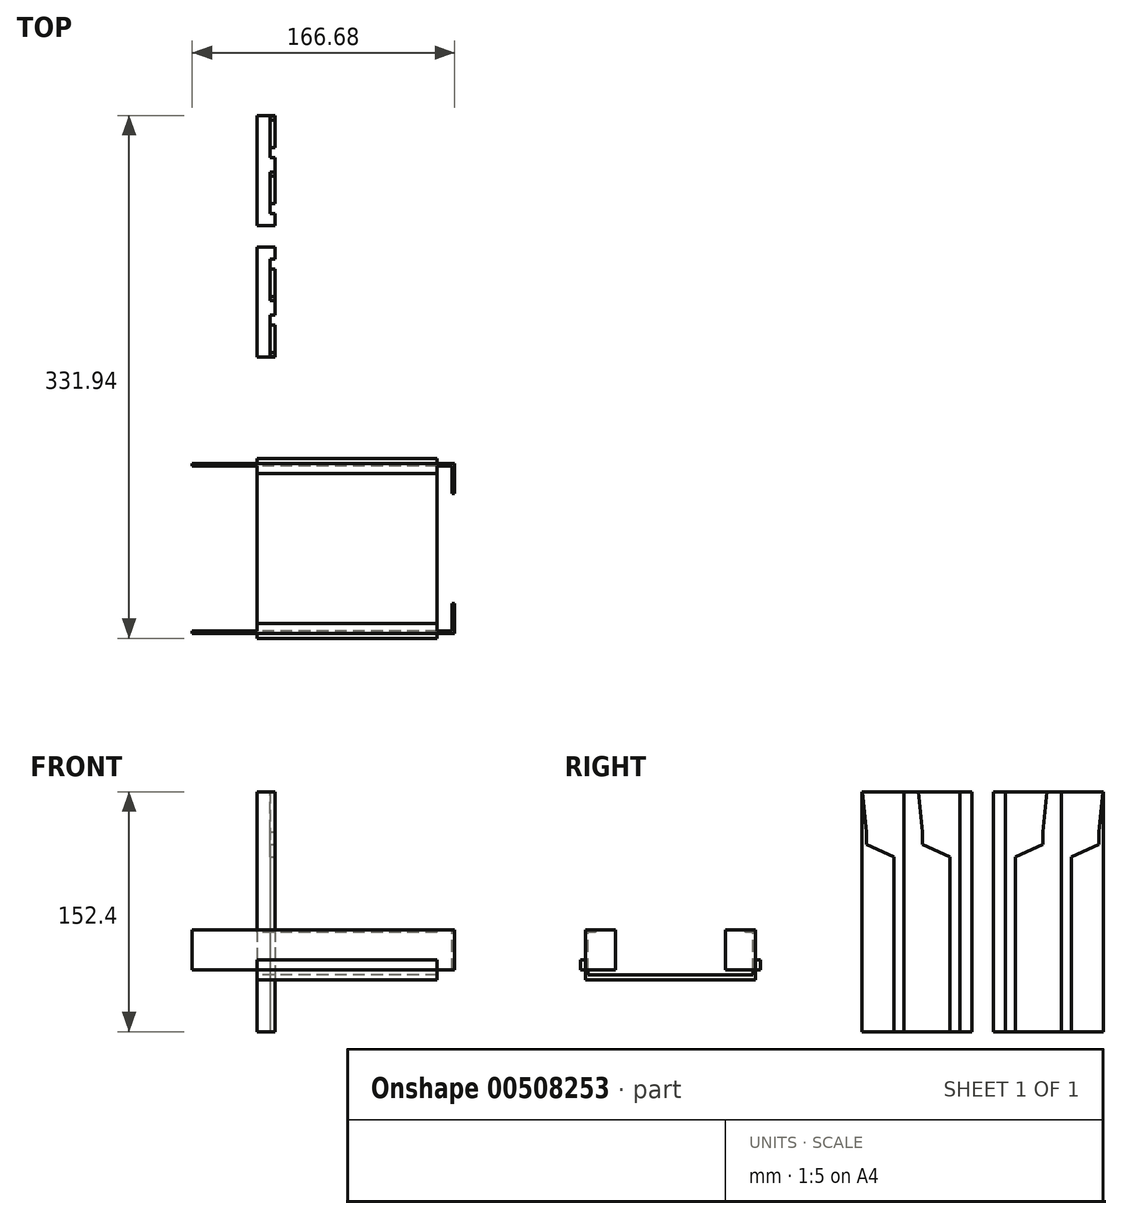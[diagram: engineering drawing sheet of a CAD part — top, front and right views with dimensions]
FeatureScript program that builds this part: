
annotation { "Feature Type Name" : "Feature", "Feature Type Description" : "" }
export const myFeature = defineFeature(function(context is Context, id is Id, definition is map)
    precondition{}
    {
        {
            var Q0;
            Q0=qCreatedBy(makeId("Right.planeOp"),FACE);
            var sketch = newSketch(context, id + "F0", { "sketchPlane" : qUnion([Q0])});
            skLineSegment(sketch, "E0.bottom", {"start": v(-76.26, 61.17) * mm, "end": v(-6.41, 61.17) * mm});
            skLineSegment(sketch, "E0.top", {"start": v(-76.26, -91.23) * mm, "end": v(-6.41, -91.23) * mm});
            skLineSegment(sketch, "E0.left", {"start": v(-76.26, 61.17) * mm, "end": v(-76.26, -91.23) * mm});
            skLineSegment(sketch, "E0.right", {"start": v(-6.41, 61.17) * mm, "end": v(-6.41, -91.23) * mm});
            skLineSegment(sketch, "E1.bottom", {"start": v(7.11, 61.17) * mm, "end": v(76.96, 61.17) * mm});
            skLineSegment(sketch, "E1.top", {"start": v(7.11, -91.23) * mm, "end": v(76.96, -91.23) * mm});
            skLineSegment(sketch, "E1.left", {"start": v(7.11, 61.17) * mm, "end": v(7.11, -91.23) * mm});
            skLineSegment(sketch, "E1.right", {"start": v(76.96, 61.17) * mm, "end": v(76.96, -91.23) * mm});
            skSolve(sketch);
        }
        {
            var Q0;
            Q0 = qSketchRegion(id + "F0", true);
            extrude(context, id + "F1", {"entities" : qUnion([Q0]), "depth" : 11.5 * mm, "offsetDistance" : 25.4 * mm});
        }
        {
            var Q0;
            Q0=makeQuery(id+"F1.opExtrude","CAP_FACE",FACE,{"disambiguationData":[OSD([sQuery(id+"F0.wireOp",EDGE,"E0.bottom"),sQuery(id+"F0.wireOp",EDGE,"E0.top"),sQuery(id+"F0.wireOp",EDGE,"E0.left"),sQuery(id+"F0.wireOp",EDGE,"E0.right")])],"isStart":false});
            var sketch = newSketch(context, id + "F2", { "sketchPlane" : qUnion([Q0])});
            skLineSegment(sketch, "E2.bottom", {"start": v(-55.94, 61.17) * mm, "end": v(-49.6, 61.17) * mm});
            skLineSegment(sketch, "E2.top", {"start": v(-55.94, -91.23) * mm, "end": v(-49.6, -91.23) * mm});
            skLineSegment(sketch, "E2.left", {"start": v(-55.94, 61.17) * mm, "end": v(-55.94, -91.23) * mm});
            skLineSegment(sketch, "E2.right", {"start": v(-49.6, 61.17) * mm, "end": v(-49.6, -91.23) * mm});
            skLineSegment(sketch, "E3.bottom", {"start": v(50.3, 61.17) * mm, "end": v(56.64, 61.17) * mm});
            skLineSegment(sketch, "E3.top", {"start": v(50.3, -91.23) * mm, "end": v(56.64, -91.23) * mm});
            skLineSegment(sketch, "E3.left", {"start": v(50.3, 61.17) * mm, "end": v(50.3, -91.23) * mm});
            skLineSegment(sketch, "E3.right", {"start": v(56.64, 61.17) * mm, "end": v(56.64, -91.23) * mm});
            skLineSegment(sketch, "E4.bottom", {"start": v(-14.03, 61.17) * mm, "end": v(-20.38, 61.17) * mm});
            skLineSegment(sketch, "E4.top", {"start": v(-14.03, -91.23) * mm, "end": v(-20.38, -91.23) * mm});
            skLineSegment(sketch, "E4.left", {"start": v(-14.03, 61.17) * mm, "end": v(-14.03, -91.23) * mm});
            skLineSegment(sketch, "E4.right", {"start": v(-20.38, 61.17) * mm, "end": v(-20.38, -91.23) * mm});
            skLineSegment(sketch, "E5.bottom", {"start": v(21.08, 61.17) * mm, "end": v(14.73, 61.17) * mm});
            skLineSegment(sketch, "E5.top", {"start": v(21.08, -91.23) * mm, "end": v(14.73, -91.23) * mm});
            skLineSegment(sketch, "E5.left", {"start": v(21.08, 61.17) * mm, "end": v(21.08, -91.23) * mm});
            skLineSegment(sketch, "E5.right", {"start": v(14.73, 61.17) * mm, "end": v(14.73, -91.23) * mm});
            skLineSegment(sketch, "E6", {"start": v(-20.38, 19.9) * mm, "end": v(-37.85, 27.83) * mm});
            skLineSegment(sketch, "E7", {"start": v(-37.85, 27.83) * mm, "end": v(-37.85, 35.77) * mm});
            skLineSegment(sketch, "E8", {"start": v(-37.85, 35.77) * mm, "end": v(-40.54, 61.17) * mm});
            skLineSegment(sketch, "E9", {"start": v(-40.54, 61.17) * mm, "end": v(-20.38, 61.17) * mm});
            skLineSegment(sketch, "E10.MirrorCS", {"start": v(38.54, 35.77) * mm, "end": v(41.24, 61.17) * mm});
            skLineSegment(sketch, "E11.MirrorCS", {"start": v(41.24, 61.17) * mm, "end": v(21.08, 61.17) * mm});
            skLineSegment(sketch, "E12.MirrorCS", {"start": v(38.54, 27.83) * mm, "end": v(38.54, 35.77) * mm});
            skLineSegment(sketch, "E13.MirrorCS", {"start": v(21.08, 19.9) * mm, "end": v(38.54, 27.83) * mm});
            skLineSegment(sketch, "E14.1.0.0", {"start": v(-76.1, 61.17) * mm, "end": v(-55.94, 61.17) * mm});
            skLineSegment(sketch, "E14.1.0.1", {"start": v(-73.4, 35.77) * mm, "end": v(-76.1, 61.17) * mm});
            skLineSegment(sketch, "E14.1.0.2", {"start": v(-73.4, 27.83) * mm, "end": v(-73.4, 35.77) * mm});
            skLineSegment(sketch, "E14.1.0.3", {"start": v(-55.94, 19.9) * mm, "end": v(-73.4, 27.83) * mm});
            skLineSegment(sketch, "E14.direction1", {"start": v(-20.38, 61.17) * mm, "end": v(-55.94, 61.17) * mm, "construction": true});
            skLineSegment(sketch, "E15.1.0.0", {"start": v(76.8, 61.17) * mm, "end": v(56.64, 61.17) * mm});
            skLineSegment(sketch, "E15.1.0.1", {"start": v(74.1, 35.77) * mm, "end": v(76.8, 61.17) * mm});
            skLineSegment(sketch, "E15.1.0.2", {"start": v(74.1, 27.83) * mm, "end": v(74.1, 35.77) * mm});
            skLineSegment(sketch, "E15.1.0.3", {"start": v(56.64, 19.9) * mm, "end": v(74.1, 27.83) * mm});
            skLineSegment(sketch, "E15.direction1", {"start": v(21.08, 61.17) * mm, "end": v(56.64, 61.17) * mm, "construction": true});
            skSolve(sketch);
        }
        {
            var Q0;
            Q0 = qSketchRegion(id + "F2", true);
            extrude(context, id + "F3", {"entities" : qUnion([Q0]), "operationType" : NewBodyOperationType.REMOVE, "oppositeDirection" : true, "depth" : 3.17 * mm, "offsetDistance" : 25.4 * mm});
        }
        {
            var Q0;
            Q0=qCreatedBy(makeId("Right.planeOp"),FACE);
            var sketch = newSketch(context, id + "F4", { "sketchPlane" : qUnion([Q0])});
            skLineSegment(sketch, "E16", {"start": v(-245.45, -28.26) * mm, "end": v(-250.21, -28.26) * mm});
            skLineSegment(sketch, "E17", {"start": v(-250.21, -28.26) * mm, "end": v(-250.21, -55.24) * mm});
            skLineSegment(sketch, "E18", {"start": v(-250.21, -55.24) * mm, "end": v(-145.44, -55.24) * mm});
            skLineSegment(sketch, "E19", {"start": v(-145.44, -55.24) * mm, "end": v(-145.44, -28.26) * mm});
            skLineSegment(sketch, "E20", {"start": v(-145.44, -28.26) * mm, "end": v(-150.2, -28.26) * mm});
            skLineSegment(sketch, "E21", {"start": v(-150.2, -28.26) * mm, "end": v(-150.2, -26.67) * mm});
            skLineSegment(sketch, "E22", {"start": v(-150.2, -26.67) * mm, "end": v(-143.85, -26.67) * mm});
            skLineSegment(sketch, "E23", {"start": v(-143.85, -26.67) * mm, "end": v(-143.85, -58.42) * mm});
            skLineSegment(sketch, "E24", {"start": v(-143.85, -58.42) * mm, "end": v(-251.8, -58.42) * mm});
            skLineSegment(sketch, "E25", {"start": v(-251.8, -58.42) * mm, "end": v(-251.8, -26.67) * mm});
            skLineSegment(sketch, "E26", {"start": v(-251.8, -26.67) * mm, "end": v(-245.45, -26.67) * mm});
            skLineSegment(sketch, "E27", {"start": v(-245.45, -26.67) * mm, "end": v(-245.45, -28.26) * mm});
            skLineSegment(sketch, "E28.bottom", {"start": v(-143.85, -52.07) * mm, "end": v(-140.68, -52.07) * mm});
            skLineSegment(sketch, "E28.top", {"start": v(-143.85, -45.72) * mm, "end": v(-140.68, -45.72) * mm});
            skLineSegment(sketch, "E28.left", {"start": v(-143.85, -52.07) * mm, "end": v(-143.85, -45.72) * mm});
            skLineSegment(sketch, "E28.right", {"start": v(-140.68, -52.07) * mm, "end": v(-140.68, -45.72) * mm});
            skLineSegment(sketch, "E29.bottom", {"start": v(-251.8, -52.07) * mm, "end": v(-254.98, -52.07) * mm});
            skLineSegment(sketch, "E29.top", {"start": v(-251.8, -45.72) * mm, "end": v(-254.98, -45.72) * mm});
            skLineSegment(sketch, "E29.left", {"start": v(-251.8, -52.07) * mm, "end": v(-251.8, -45.72) * mm});
            skLineSegment(sketch, "E29.right", {"start": v(-254.98, -52.07) * mm, "end": v(-254.98, -45.72) * mm});
            skSolve(sketch);
        }
        {
            var Q0;
            Q0 = qSketchRegion(id + "F4", true);
            extrude(context, id + "F5", {"entities" : qUnion([Q0]), "depth" : 114.3 * mm, "offsetDistance" : 25.4 * mm});
        }
        {
            var Q0;
            Q0=makeQuery(id+"F5.opExtrude","SWEPT_FACE",FACE,{"disambiguationData":[OSD([sQuery(id+"F4.wireOp",EDGE,"E26")])]});
            var sketch = newSketch(context, id + "F6", { "sketchPlane" : qUnion([Q0])});
            skLineSegment(sketch, "E30", {"start": v(114.3, -143.85) * mm, "end": v(125.41, -143.85) * mm});
            skLineSegment(sketch, "E31", {"start": v(125.41, -143.85) * mm, "end": v(125.41, -162.9) * mm});
            skLineSegment(sketch, "E32", {"start": v(125.41, -162.9) * mm, "end": v(123.83, -162.9) * mm});
            skLineSegment(sketch, "E33", {"start": v(123.83, -162.9) * mm, "end": v(123.83, -145.44) * mm});
            skLineSegment(sketch, "E34", {"start": v(123.83, -145.44) * mm, "end": v(114.3, -145.44) * mm});
            skLineSegment(sketch, "E35", {"start": v(114.3, -145.44) * mm, "end": v(114.3, -143.85) * mm});
            skLineSegment(sketch, "E36", {"start": v(114.3, -251.8) * mm, "end": v(125.41, -251.8) * mm});
            skLineSegment(sketch, "E37", {"start": v(125.41, -251.8) * mm, "end": v(125.41, -232.75) * mm});
            skLineSegment(sketch, "E38", {"start": v(125.41, -232.75) * mm, "end": v(123.83, -232.75) * mm});
            skLineSegment(sketch, "E39", {"start": v(123.83, -232.75) * mm, "end": v(123.83, -250.21) * mm});
            skLineSegment(sketch, "E40", {"start": v(123.83, -250.21) * mm, "end": v(114.3, -250.21) * mm});
            skLineSegment(sketch, "E41", {"start": v(114.3, -250.21) * mm, "end": v(114.3, -251.8) * mm});
            skLineSegment(sketch, "E42.bottom", {"start": v(0, -143.85) * mm, "end": v(-41.28, -143.85) * mm});
            skLineSegment(sketch, "E42.top", {"start": v(0, -145.44) * mm, "end": v(-41.28, -145.44) * mm});
            skLineSegment(sketch, "E42.left", {"start": v(0, -143.85) * mm, "end": v(0, -145.44) * mm});
            skLineSegment(sketch, "E42.right", {"start": v(-41.28, -143.85) * mm, "end": v(-41.28, -145.44) * mm});
            skLineSegment(sketch, "E43.bottom", {"start": v(0, -251.8) * mm, "end": v(-41.28, -251.8) * mm});
            skLineSegment(sketch, "E43.top", {"start": v(0, -250.21) * mm, "end": v(-41.28, -250.21) * mm});
            skLineSegment(sketch, "E43.left", {"start": v(0, -251.8) * mm, "end": v(0, -250.21) * mm});
            skLineSegment(sketch, "E43.right", {"start": v(-41.28, -251.8) * mm, "end": v(-41.28, -250.21) * mm});
            skSolve(sketch);
        }
        {
            var Q0;
            Q0 = qSketchRegion(id + "F6", true);
            extrude(context, id + "F7", {"entities" : qUnion([Q0]), "operationType" : NewBodyOperationType.ADD, "oppositeDirection" : true, "depth" : 25.4 * mm, "offsetDistance" : 25.4 * mm});
        }
    });
